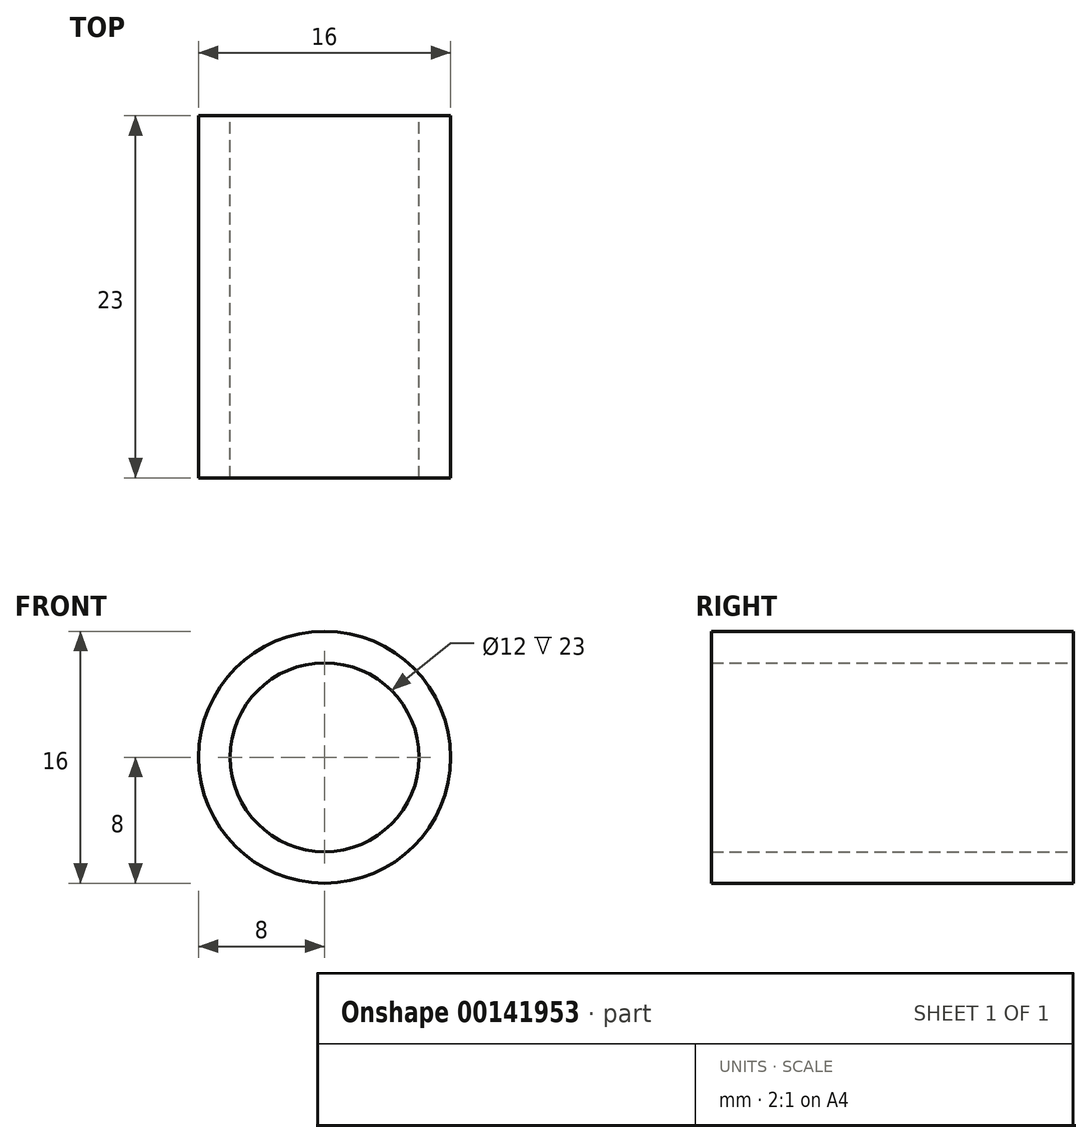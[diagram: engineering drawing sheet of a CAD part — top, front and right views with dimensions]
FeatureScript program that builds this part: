
annotation { "Feature Type Name" : "Feature", "Feature Type Description" : "" }
export const myFeature = defineFeature(function(context is Context, id is Id, definition is map)
    precondition{}
    {
        {
            var Q0;
            Q0=qCreatedBy(makeId("Front.planeOp"),FACE);
            var sketch = newSketch(context, id + "F0", { "sketchPlane" : qUnion([Q0])});
            skCircle(sketch, "E0", {"center": v(0, 0) * mm, "radius": 6 * mm});
            skCircle(sketch, "E1", {"center": v(0, 0) * mm, "radius": 8 * mm});
            skSolve(sketch);
        }
        {
            var Q0;
            Q0=makeQuery(id+"F0.imprint","IMPRINT",FACE,{"disambiguationData":[TD([[makeQuery(id+"F0.imprint","IMPRINT",EDGE,{"derivedFrom":sQuery(id+"F0.wireOp",EDGE,"E0")}),-1.0]])]});
            extrude(context, id + "F1", {"entities" : qUnion([Q0]), "depth" : 23 * mm, "offsetDistance" : 25 * mm});
        }
    });
